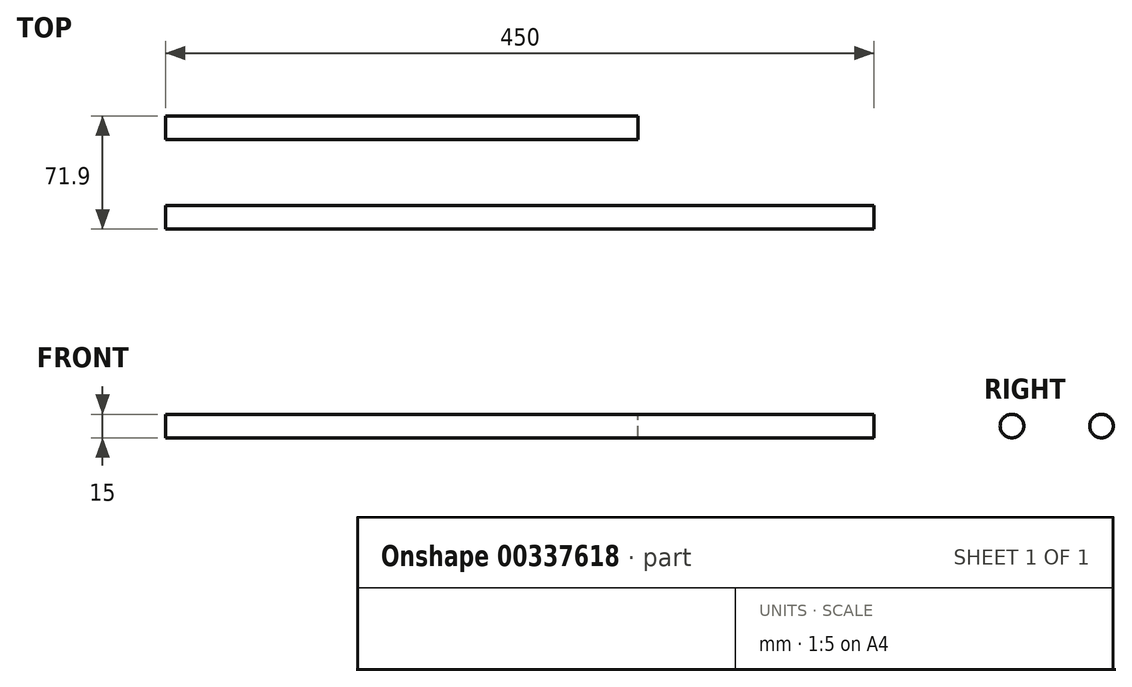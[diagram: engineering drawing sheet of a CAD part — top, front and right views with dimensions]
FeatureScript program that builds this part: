
annotation { "Feature Type Name" : "Feature", "Feature Type Description" : "" }
export const myFeature = defineFeature(function(context is Context, id is Id, definition is map)
    precondition{}
    {
        {
            var Q0;
            Q0=qCreatedBy(makeId("Right.planeOp"),FACE);
            var sketch = newSketch(context, id + "F0", { "sketchPlane" : qUnion([Q0])});
            skCircle(sketch, "E0", {"center": v(0, 0) * mm, "radius": 7.5 * mm});
            skSolve(sketch);
        }
        {
            var Q0;
            Q0=makeQuery(id+"F0.imprint","IMPRINT",FACE,{"disambiguationData":[TD([[makeQuery(id+"F0.imprint","IMPRINT",EDGE,{"derivedFrom":sQuery(id+"F0.wireOp",EDGE,"E0")}),1.0]])]});
            extrude(context, id + "F1", {"entities" : qUnion([Q0]), "depth" : 300 * mm});
        }
        {
            var Q0;
            Q0=qCreatedBy(makeId("Right.planeOp"),FACE);
            var sketch = newSketch(context, id + "F2", { "sketchPlane" : qUnion([Q0])});
            skCircle(sketch, "E1", {"center": v(-56.9, 0) * mm, "radius": 7.5 * mm});
            skSolve(sketch);
        }
        {
            var Q0;
            Q0=makeQuery(id+"F2.imprint","IMPRINT",FACE,{"disambiguationData":[TD([[makeQuery(id+"F2.imprint","IMPRINT",EDGE,{"derivedFrom":sQuery(id+"F2.wireOp",EDGE,"E1")}),1.0]])]});
            extrude(context, id + "F3", {"entities" : qUnion([Q0]), "depth" : 450 * mm});
        }
    });
